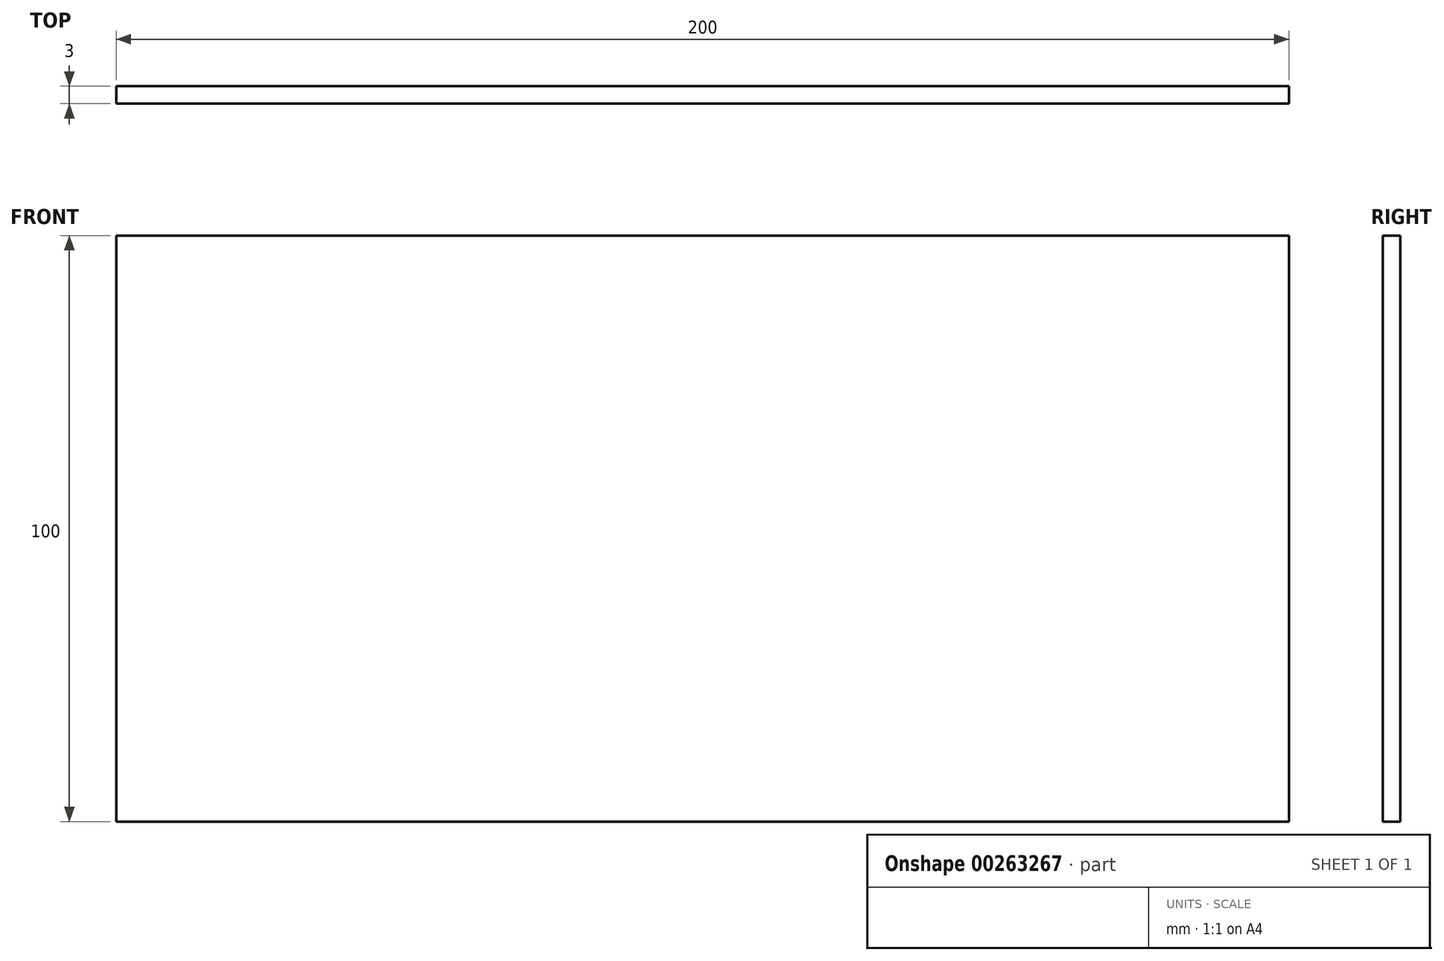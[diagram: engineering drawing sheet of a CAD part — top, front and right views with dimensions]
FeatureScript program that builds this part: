
annotation { "Feature Type Name" : "Feature", "Feature Type Description" : "" }
export const myFeature = defineFeature(function(context is Context, id is Id, definition is map)
    precondition{}
    {
        {
            var Q0;
            Q0=qCreatedBy(makeId("Front.planeOp"),FACE);
            var sketch = newSketch(context, id + "F0", { "sketchPlane" : qUnion([Q0])});
            skLineSegment(sketch, "E0.bottom", {"start": v(100, -50) * mm, "end": v(-100, -50) * mm});
            skLineSegment(sketch, "E0.top", {"start": v(100, 50) * mm, "end": v(-100, 50) * mm});
            skLineSegment(sketch, "E0.left", {"start": v(100, -50) * mm, "end": v(100, 50) * mm});
            skLineSegment(sketch, "E0.right", {"start": v(-100, -50) * mm, "end": v(-100, 50) * mm});
            skPoint(sketch, "E0.middle", {"position": v(0, 0) * mm});
            skSolve(sketch);
        }
        {
            var Q0;
            Q0 = qSketchRegion(id + "F0", true);
            extrude(context, id + "F1", {"entities" : qUnion([Q0]), "depth" : 3 * mm});
        }
    });
